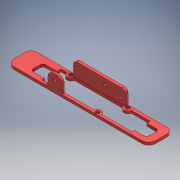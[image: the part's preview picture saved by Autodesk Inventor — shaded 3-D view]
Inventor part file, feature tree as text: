
AUTODESK INVENTOR PART (.ipt)
format: ipt  version: 2017 (Build 210142000, 142)  size: 409,600 bytes
history: native  units: mm
features: reference x14, sketch x6, extrude x4, fillet x4, projected_geometry x4, other x4, hole x2
ambient origin geometry x8: Origin, YZ Plane, XZ Plane, XY Plane, X Axis, Y Axis, Z Axis, Center Point
bodies: Solid1 (feature_tree)
feature tree (38):
  extrude  "Extrusion1"  Depth=4.5mm
  hole  "Hole1"  [1 undecoded]
  extrude  "Extrusion2"  Depth=7.75mm
  fillet  "Fillet1"  Radius=20.6mm
  extrude  "Extrusion3"  Depth=3.0mm TaperAngle=0.0deg
  extrude  "Extrusion4"  Depth=4.0mm
  fillet  "Fillet3"  Radius=3.25mm
  fillet  "Fillet4"  Radius=16.0mm
  fillet  "Fillet5"  Radius=6.5mm
  hole  "Hole2"  [1 undecoded]
  sketch  "Sketch1"  dims[d0=3.0mm d1=0.0mm]
  reference  "Reference1"
  reference  "Reference2"
  reference  "Reference3"
  sketch  "Sketch2"  dims[d2=2.3mm d3=6.0mm d4=4.5mm d5=2.2mm d6=90.0deg d7=8.0mm d8=20.594885mm d9=4.5mm]
  reference  "Reference4"
  reference  "Reference5"
  reference  "Reference6"
  sketch  "Sketch3"  dims[d10=4.5mm d11=4.5mm]
  projected_geometry  "Projected Loop1"
  projected_geometry  "Projected Loop2"
  projected_geometry  "Projected Loop3"
  reference  "Reference7"
  reference  "Reference8"
  reference  "Reference9"
  reference  "Reference10"
  reference  "Reference11"
  reference  "Reference12"
  reference  "Reference13"
  reference  "Reference14"
  sketch  "Sketch4"  dims[d12=3.0mm d13=0.0mm d14=7.75mm d15=20.6mm]
  sketch  "Sketch5"  dims[d16=16.0mm d17=3.0mm d18=0.0mm]
  projected_geometry  "Projected Loop4"
  sketch  "Sketch7"  dims[d21=2.5mm d22=0.0mm d23=4.0mm d24=3.25mm d25=16.0mm d26=6.5mm d27=3.2mm d28=6.0mm d29=4.5mm d30=2.2mm d31=90.0deg d32=8.0mm d33=20.594885mm]
  other  "<userpath>\Dropbox\Work\HeadSLAM\xtion_custom_assembly_v2_heatsink_mod.iam"
  other  "xtion_custom_assembly_v2_heatsink_mod.iam"
  other  "head_mount_v2:1"
  other  "xtion_mainboard:1"
note: 2 required parameter values undecoded (feature->parameter linkage not recoverable at this tier; creation-order binding heuristic only, values carry confidence <= 0.55)
